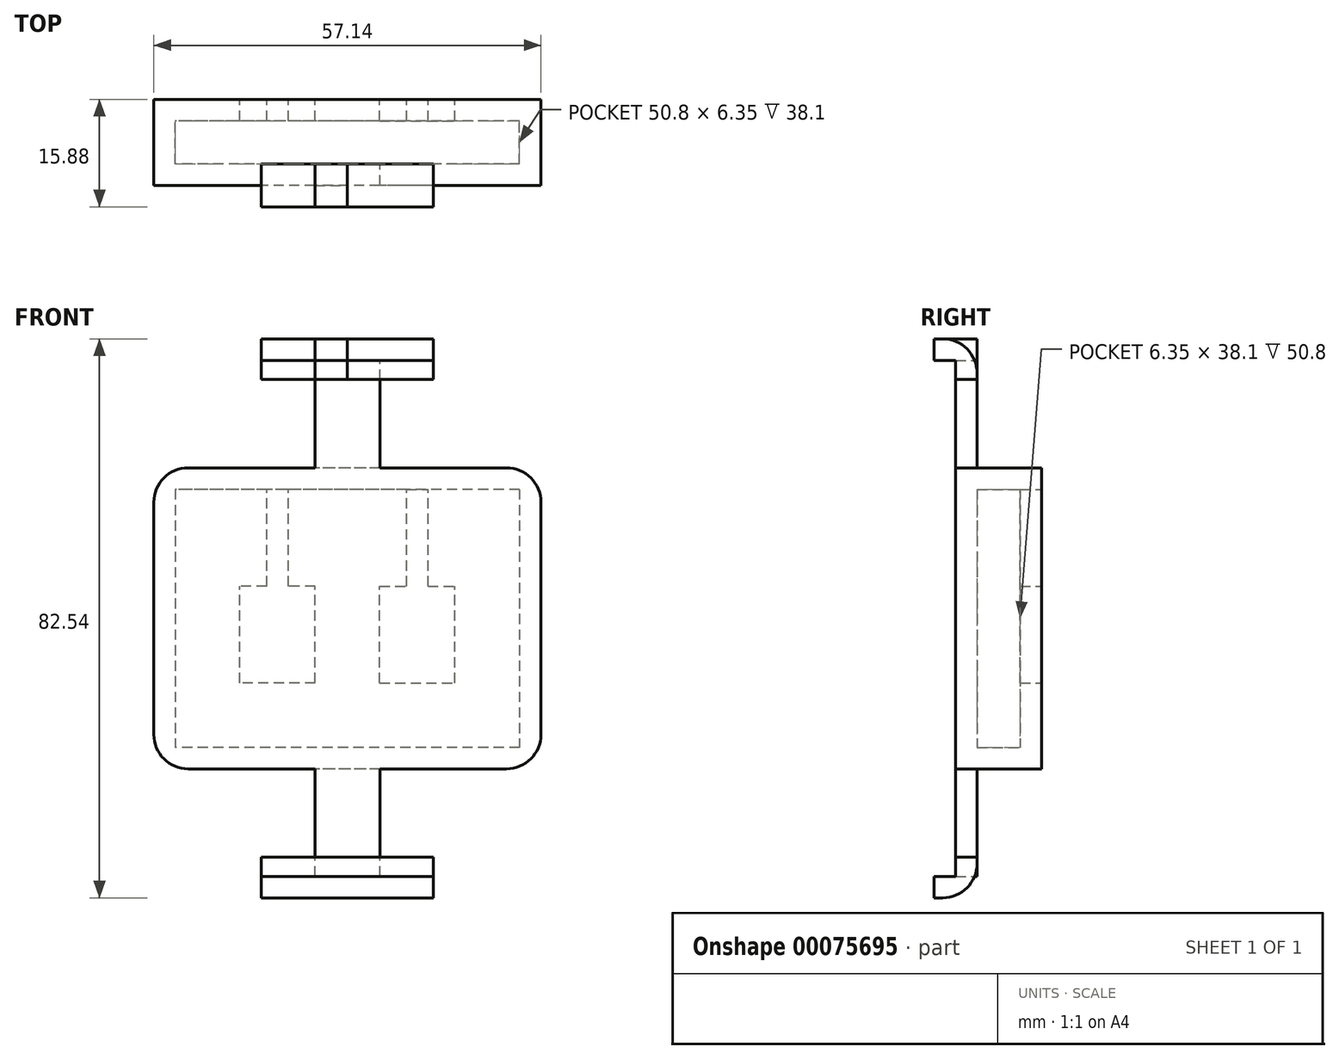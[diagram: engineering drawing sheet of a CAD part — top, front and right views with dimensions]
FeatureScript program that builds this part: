
annotation { "Feature Type Name" : "Feature", "Feature Type Description" : "" }
export const myFeature = defineFeature(function(context is Context, id is Id, definition is map)
    precondition{}
    {
        {
            var Q0;
            Q0=qCreatedBy(makeId("Front.planeOp"),FACE);
            var sketch = newSketch(context, id + "F0", { "sketchPlane" : qUnion([Q0])});
            skLineSegment(sketch, "E0.rect.bottom", {"start": v(25.4, 19.05) * mm, "end": v(-25.4, 19.05) * mm});
            skLineSegment(sketch, "E0.rect.top", {"start": v(25.4, -19.05) * mm, "end": v(-25.4, -19.05) * mm});
            skLineSegment(sketch, "E0.rect.left", {"start": v(25.4, 19.05) * mm, "end": v(25.4, -19.05) * mm});
            skLineSegment(sketch, "E0.rect.right", {"start": v(-25.4, 19.05) * mm, "end": v(-25.4, -19.05) * mm});
            skPoint(sketch, "E0.rect.middle", {"position": v(0, 0) * mm});
            skLineSegment(sketch, "E1.0", {"start": v(28.57, 22.23) * mm, "end": v(-28.58, 22.23) * mm});
            skLineSegment(sketch, "E1.1", {"start": v(28.57, 22.23) * mm, "end": v(28.58, -22.23) * mm});
            skLineSegment(sketch, "E1.2", {"start": v(28.58, -22.23) * mm, "end": v(-28.57, -22.23) * mm});
            skLineSegment(sketch, "E1.3", {"start": v(-28.58, 22.23) * mm, "end": v(-28.57, -22.23) * mm});
            skSolve(sketch);
        }
        {
            var Q0;
            Q0 = qSketchRegion(id + "F0", true);
            extrude(context, id + "F1", {"entities" : qUnion([Q0]), "depth" : 6.35 * mm});
        }
        {
            var Q0;
            Q0=makeQuery(id+"F1.opExtrude","SWEPT_EDGE",EDGE,{"disambiguationData":[OSD([sQuery(id+"F0.wireOp",EDGE,"E1.0"),sQuery(id+"F0.wireOp",EDGE,"E1.3")])]});
            var Q1;
            Q1=makeQuery(id+"F1.opExtrude","SWEPT_EDGE",EDGE,{"disambiguationData":[OSD([sQuery(id+"F0.wireOp",EDGE,"E1.0"),sQuery(id+"F0.wireOp",EDGE,"E1.1")])]});
            var Q2;
            Q2=makeQuery(id+"F1.opExtrude","SWEPT_EDGE",EDGE,{"disambiguationData":[OSD([sQuery(id+"F0.wireOp",EDGE,"E1.1"),sQuery(id+"F0.wireOp",EDGE,"E1.2")])]});
            var Q3;
            Q3=makeQuery(id+"F1.opExtrude","SWEPT_EDGE",EDGE,{"disambiguationData":[OSD([sQuery(id+"F0.wireOp",EDGE,"E1.2"),sQuery(id+"F0.wireOp",EDGE,"E1.3")])]});
            fillet(context, id + "F2", {"entities" : qUnion([Q0, Q1, Q2, Q3]), "radius" : 5.08 * mm, "tangentPropagation" : true, "allowEdgeOverflow" : false});
        }
        {
            var Q0;
            Q0=makeQuery(id+"F1.opExtrude","CAP_FACE",FACE,{"disambiguationData":[OSD([sQuery(id+"F0.wireOp",EDGE,"E0.rect.bottom"),sQuery(id+"F0.wireOp",EDGE,"E0.rect.top"),sQuery(id+"F0.wireOp",EDGE,"E0.rect.left"),sQuery(id+"F0.wireOp",EDGE,"E0.rect.right"),sQuery(id+"F0.wireOp",EDGE,"E1.0"),sQuery(id+"F0.wireOp",EDGE,"E1.1"),sQuery(id+"F0.wireOp",EDGE,"E1.2"),sQuery(id+"F0.wireOp",EDGE,"E1.3")])],"isStart":true});
            var sketch = newSketch(context, id + "F3", { "sketchPlane" : qUnion([Q0])});
            skLineSegment(sketch, "E2.0", {"start": v(-23.5, 22.23) * mm, "end": v(23.5, 22.23) * mm});
            skArc(sketch, "E3.0", {"start": v(28.58, 17.14) * mm, "mid": v(27.09, 20.74) * mm, "end": v(23.5, 22.22) * mm});
            skLineSegment(sketch, "E4.0", {"start": v(28.58, 17.14) * mm, "end": v(28.57, -17.15) * mm});
            skArc(sketch, "E5.0", {"start": v(23.5, -22.23) * mm, "mid": v(27.09, -20.74) * mm, "end": v(28.57, -17.15) * mm});
            skLineSegment(sketch, "E6.0", {"start": v(-23.5, -22.23) * mm, "end": v(23.5, -22.23) * mm});
            skArc(sketch, "E7.0", {"start": v(-28.58, -17.15) * mm, "mid": v(-27.09, -20.74) * mm, "end": v(-23.5, -22.23) * mm});
            skLineSegment(sketch, "E8.0", {"start": v(-28.57, 17.14) * mm, "end": v(-28.58, -17.15) * mm});
            skArc(sketch, "E9.0", {"start": v(-23.5, 22.23) * mm, "mid": v(-27.09, 20.74) * mm, "end": v(-28.57, 17.14) * mm});
            skSolve(sketch);
        }
        {
            var Q0;
            Q0 = qSketchRegion(id + "F3", true);
            extrude(context, id + "F4", {"entities" : qUnion([Q0]), "operationType" : NewBodyOperationType.ADD, "depth" : 3.17 * mm});
        }
        {
            var Q0;
            Q0=makeQuery(id+"F4.opExtrude","CAP_FACE",FACE,{"disambiguationData":[OSD([sQuery(id+"F3.wireOp",EDGE,"E2.0"),sQuery(id+"F3.wireOp",EDGE,"E3.0"),sQuery(id+"F3.wireOp",EDGE,"E4.0"),sQuery(id+"F3.wireOp",EDGE,"E5.0"),sQuery(id+"F3.wireOp",EDGE,"E6.0"),sQuery(id+"F3.wireOp",EDGE,"E7.0"),sQuery(id+"F3.wireOp",EDGE,"E8.0"),sQuery(id+"F3.wireOp",EDGE,"E9.0")])],"isStart":false});
            var sketch = newSketch(context, id + "F5", { "sketchPlane" : qUnion([Q0])});
            skLineSegment(sketch, "E10.rect.top", {"start": v(-8.73, 19.05) * mm, "end": v(-11.9, 19.05) * mm});
            skLineSegment(sketch, "E10.rect.left", {"start": v(-8.73, 4.75) * mm, "end": v(-8.73, 19.05) * mm});
            skLineSegment(sketch, "E10.rect.right", {"start": v(-11.9, 4.75) * mm, "end": v(-11.9, 19.05) * mm});
            skLineSegment(sketch, "E11.rect.bottom", {"start": v(-4.76, -9.54) * mm, "end": v(-15.88, -9.54) * mm});
            skLineSegment(sketch, "E11.rect.top", {"start": v(-4.76, 4.75) * mm, "end": v(-8.73, 4.75) * mm});
            skLineSegment(sketch, "E11.rect.left", {"start": v(-4.76, -9.54) * mm, "end": v(-4.76, 4.75) * mm});
            skLineSegment(sketch, "E11.rect.right", {"start": v(-15.88, -9.54) * mm, "end": v(-15.88, 4.75) * mm});
            skLineSegment(sketch, "E12.trimOffspring", {"start": v(-11.9, 4.75) * mm, "end": v(-15.88, 4.75) * mm});
            skPoint(sketch, "E13.endSnap0", {"position": v(0, 22.23) * mm});
            skLineSegment(sketch, "E14.MirrorCS", {"start": v(11.9, 4.75) * mm, "end": v(15.88, 4.75) * mm});
            skLineSegment(sketch, "E15.MirrorCS", {"start": v(8.73, 19.05) * mm, "end": v(11.9, 19.05) * mm});
            skLineSegment(sketch, "E16.MirrorCS", {"start": v(4.76, 4.75) * mm, "end": v(8.73, 4.75) * mm});
            skLineSegment(sketch, "E17.MirrorCS", {"start": v(11.9, 4.75) * mm, "end": v(11.9, 19.05) * mm});
            skLineSegment(sketch, "E18.MirrorCS", {"start": v(4.76, -9.54) * mm, "end": v(15.88, -9.54) * mm});
            skLineSegment(sketch, "E19.MirrorCS", {"start": v(15.88, -9.54) * mm, "end": v(15.88, 4.75) * mm});
            skLineSegment(sketch, "E20.MirrorCS", {"start": v(8.73, 4.75) * mm, "end": v(8.73, 19.05) * mm});
            skLineSegment(sketch, "E21.MirrorCS", {"start": v(4.76, -9.54) * mm, "end": v(4.76, 4.75) * mm});
            skSolve(sketch);
        }
        {
            var Q0;
            Q0 = qSketchRegion(id + "F5", true);
            extrude(context, id + "F6", {"entities" : qUnion([Q0]), "operationType" : NewBodyOperationType.REMOVE, "oppositeDirection" : true, "depth" : 25.4 * mm});
        }
        {
            var Q0;
            Q0=makeQuery(id+"F1.opExtrude","CAP_FACE",FACE,{"disambiguationData":[OSD([sQuery(id+"F0.wireOp",EDGE,"E0.rect.bottom"),sQuery(id+"F0.wireOp",EDGE,"E0.rect.top"),sQuery(id+"F0.wireOp",EDGE,"E0.rect.left"),sQuery(id+"F0.wireOp",EDGE,"E0.rect.right"),sQuery(id+"F0.wireOp",EDGE,"E1.0"),sQuery(id+"F0.wireOp",EDGE,"E1.1"),sQuery(id+"F0.wireOp",EDGE,"E1.2"),sQuery(id+"F0.wireOp",EDGE,"E1.3")])],"isStart":false});
            var sketch = newSketch(context, id + "F7", { "sketchPlane" : qUnion([Q0])});
            skArc(sketch, "E22.0", {"start": v(-23.5, 22.22) * mm, "mid": v(-27.09, 20.74) * mm, "end": v(-28.58, 17.14) * mm});
            skLineSegment(sketch, "E23.0", {"start": v(23.5, 22.23) * mm, "end": v(4.8, 22.23) * mm});
            skArc(sketch, "E24.0", {"start": v(28.57, 17.14) * mm, "mid": v(27.09, 20.74) * mm, "end": v(23.5, 22.23) * mm});
            skLineSegment(sketch, "E25.0", {"start": v(28.57, 17.14) * mm, "end": v(28.58, -17.15) * mm});
            skArc(sketch, "E26.0", {"start": v(23.5, -22.23) * mm, "mid": v(27.09, -20.74) * mm, "end": v(28.58, -17.15) * mm});
            skLineSegment(sketch, "E27.0", {"start": v(23.5, -22.23) * mm, "end": v(4.8, -22.23) * mm});
            skArc(sketch, "E28.0", {"start": v(-28.57, -17.15) * mm, "mid": v(-27.09, -20.74) * mm, "end": v(-23.5, -22.23) * mm});
            skLineSegment(sketch, "E29.0", {"start": v(-28.58, 17.14) * mm, "end": v(-28.57, -17.15) * mm});
            skLineSegment(sketch, "E30.rect.bottom", {"start": v(4.8, -38.1) * mm, "end": v(-4.8, -38.1) * mm});
            skLineSegment(sketch, "E30.rect.top", {"start": v(4.8, 38.1) * mm, "end": v(-4.8, 38.1) * mm});
            skLineSegment(sketch, "E30.rect.left", {"start": v(4.8, -38.1) * mm, "end": v(4.8, -22.23) * mm});
            skLineSegment(sketch, "E30.rect.right", {"start": v(-4.8, -38.1) * mm, "end": v(-4.8, -22.23) * mm});
            skPoint(sketch, "E30.rect.middle", {"position": v(0, 0) * mm});
            skLineSegment(sketch, "E31.trimOffspring", {"start": v(-4.8, 22.23) * mm, "end": v(-4.8, 38.1) * mm});
            skLineSegment(sketch, "E32.trimOffspring", {"start": v(4.8, 22.23) * mm, "end": v(4.8, 38.1) * mm});
            skLineSegment(sketch, "E33.trimOffspring", {"start": v(-4.8, 22.23) * mm, "end": v(-23.5, 22.23) * mm});
            skLineSegment(sketch, "E34.trimOffspring", {"start": v(-4.8, -22.23) * mm, "end": v(-23.5, -22.23) * mm});
            skSolve(sketch);
        }
        {
            var Q0;
            Q0 = qSketchRegion(id + "F7", true);
            extrude(context, id + "F8", {"entities" : qUnion([Q0]), "operationType" : NewBodyOperationType.ADD, "depth" : 3.17 * mm});
        }
        {
            var Q0;
            Q0=qCreatedBy(makeId("Right.planeOp"),FACE);
            var sketch = newSketch(context, id + "F9", { "sketchPlane" : qUnion([Q0])});
            skLineSegment(sketch, "E35.bottom", {"start": v(-9.55, 38.1) * mm, "end": v(-12.7, 38.1) * mm});
            skLineSegment(sketch, "E35.top", {"start": v(-6.35, 41.27) * mm, "end": v(-12.7, 41.27) * mm});
            skLineSegment(sketch, "E35.left", {"start": v(-6.35, 41.27) * mm, "end": v(-6.35, 38.1) * mm});
            skLineSegment(sketch, "E35.right", {"start": v(-12.7, 41.27) * mm, "end": v(-12.7, 38.1) * mm});
            skLineSegment(sketch, "E36.top", {"start": v(-6.35, 35.27) * mm, "end": v(-9.55, 35.27) * mm});
            skLineSegment(sketch, "E36.left", {"start": v(-6.35, 38.1) * mm, "end": v(-6.35, 35.27) * mm});
            skLineSegment(sketch, "E36.right", {"start": v(-9.55, 38.1) * mm, "end": v(-9.55, 35.27) * mm});
            skLineSegment(sketch, "E37", {"start": v(0, 0) * mm, "end": v(43.76, 0) * mm});
            skLineSegment(sketch, "E38.MirrorCS", {"start": v(-6.35, -41.27) * mm, "end": v(-6.35, -38.1) * mm});
            skLineSegment(sketch, "E39.MirrorCS", {"start": v(-12.7, -41.27) * mm, "end": v(-12.7, -38.1) * mm});
            skLineSegment(sketch, "E40.MirrorCS", {"start": v(-6.35, -35.27) * mm, "end": v(-9.55, -35.27) * mm});
            skLineSegment(sketch, "E41.MirrorCS", {"start": v(-6.35, -38.1) * mm, "end": v(-6.35, -35.27) * mm});
            skLineSegment(sketch, "E42.MirrorCS", {"start": v(-9.55, -38.1) * mm, "end": v(-12.7, -38.1) * mm});
            skLineSegment(sketch, "E43.MirrorCS", {"start": v(-9.55, -38.1) * mm, "end": v(-9.55, -35.27) * mm});
            skLineSegment(sketch, "E44.MirrorCS", {"start": v(-6.35, -41.27) * mm, "end": v(-12.7, -41.27) * mm});
            skSolve(sketch);
        }
        {
            var Q0;
            Q0=makeQuery(id+"F9.imprint","IMPRINT",FACE,{"disambiguationData":[TD([[makeQuery(id+"F9.imprint","IMPRINT",EDGE,{"derivedFrom":sQuery(id+"F9.wireOp",EDGE,"E35.top")}),1.0]])]});
            var Q1;
            Q1=makeQuery(id+"F8.opExtrude","SWEPT_FACE",FACE,{"disambiguationData":[OSD([sQuery(id+"F7.wireOp",EDGE,"E31.trimOffspring")])]});
            extrude(context, id + "F10", {"entities" : qUnion([Q0]), "endBound" : BoundingType.UP_TO_SURFACE, "oppositeDirection" : true, "endBoundEntityFace" : qUnion([Q1]), "depth" : 25.4 * mm});
        }
        {
            var Q0;
            Q0 = qSketchRegion(id + "F9", true);
            extrude(context, id + "F11", {"entities" : qUnion([Q0]), "depth" : 12.7 * mm, "hasSecondDirection" : true, "secondDirectionOppositeDirection" : true, "secondDirectionDepth" : 12.7 * mm});
        }
        {
            var Q0;
            Q0=makeQuery(id+"F11.opExtrude","SWEPT_EDGE",EDGE,{"disambiguationData":[OSD([sQuery(id+"F9.wireOp",EDGE,"E35.top"),sQuery(id+"F9.wireOp",EDGE,"E35.left")])]});
            var Q1;
            Q1=makeQuery(id+"F11.opExtrude","SWEPT_EDGE",EDGE,{"disambiguationData":[OSD([sQuery(id+"F9.wireOp",EDGE,"E38.MirrorCS"),sQuery(id+"F9.wireOp",EDGE,"E44.MirrorCS")])]});
            fillet(context, id + "F12", {"entities" : qUnion([Q0, Q1]), "radius" : 5.08 * mm, "tangentPropagation" : true, "allowEdgeOverflow" : false});
        }
    });
